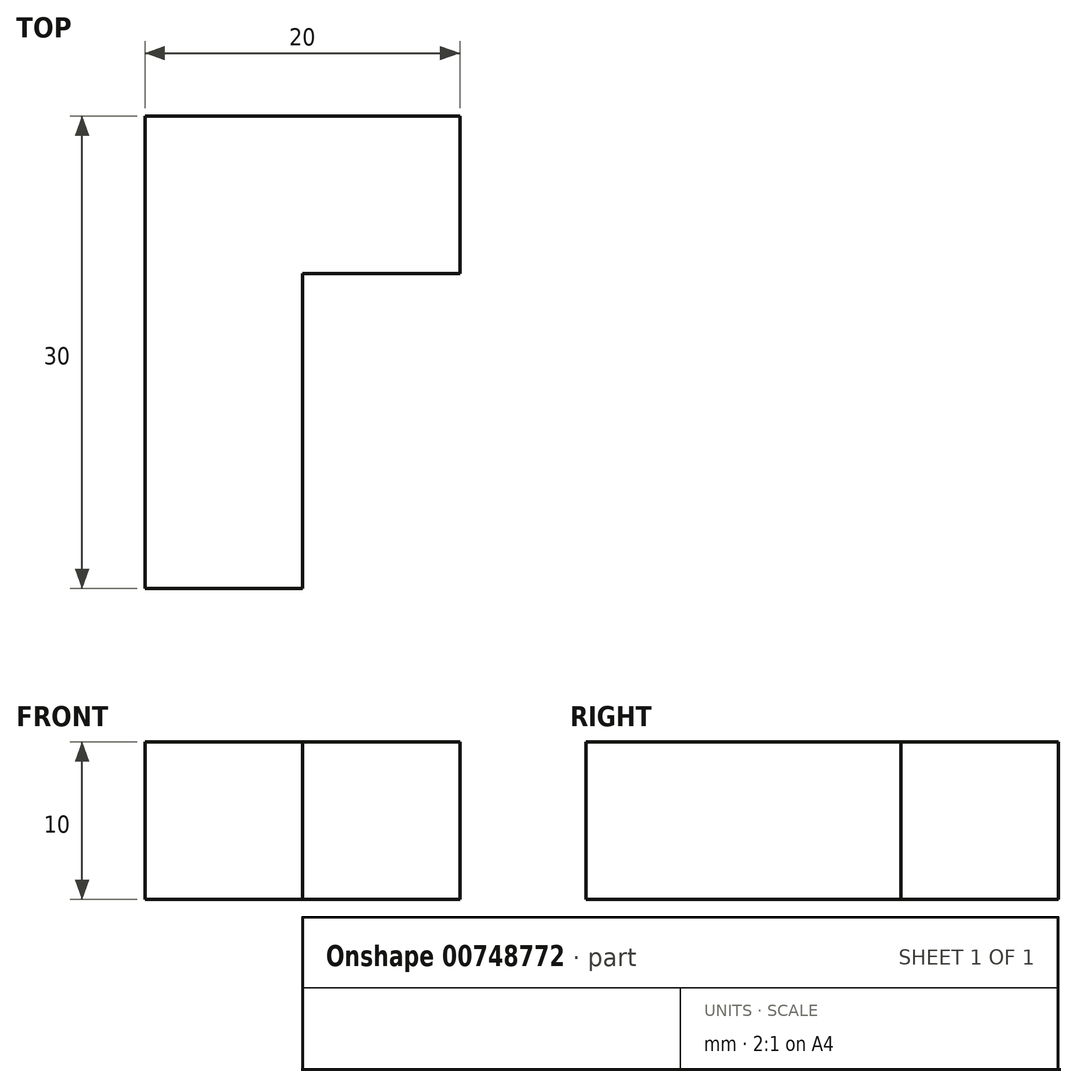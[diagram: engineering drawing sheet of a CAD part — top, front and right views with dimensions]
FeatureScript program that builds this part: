
annotation { "Feature Type Name" : "Feature", "Feature Type Description" : "" }
export const myFeature = defineFeature(function(context is Context, id is Id, definition is map)
    precondition{}
    {
        {
            var Q0;
            Q0=qCreatedBy(makeId("Top.planeOp"),FACE);
            var sketch = newSketch(context, id + "F0", { "sketchPlane" : qUnion([Q0])});
            skLineSegment(sketch, "E0.bottom", {"start": v(-49.52, 42.56) * mm, "end": v(-39.52, 42.56) * mm});
            skLineSegment(sketch, "E0.top", {"start": v(-49.52, 32.56) * mm, "end": v(-39.52, 32.56) * mm});
            skLineSegment(sketch, "E0.left", {"start": v(-49.52, 42.56) * mm, "end": v(-49.52, 32.56) * mm});
            skLineSegment(sketch, "E0.right", {"start": v(-39.52, 42.56) * mm, "end": v(-39.52, 32.56) * mm});
            skLineSegment(sketch, "E1.bottom", {"start": v(-39.52, 42.56) * mm, "end": v(-29.52, 42.56) * mm});
            skLineSegment(sketch, "E1.top", {"start": v(-39.52, 32.56) * mm, "end": v(-29.52, 32.56) * mm});
            skLineSegment(sketch, "E1.right", {"start": v(-29.52, 42.56) * mm, "end": v(-29.52, 32.56) * mm});
            skLineSegment(sketch, "E2.top", {"start": v(-49.52, 22.56) * mm, "end": v(-39.52, 22.56) * mm});
            skLineSegment(sketch, "E2.left", {"start": v(-49.52, 32.56) * mm, "end": v(-49.52, 22.56) * mm});
            skLineSegment(sketch, "E2.right", {"start": v(-39.52, 32.56) * mm, "end": v(-39.52, 22.56) * mm});
            skLineSegment(sketch, "E3.top", {"start": v(-49.52, 12.56) * mm, "end": v(-39.52, 12.56) * mm});
            skLineSegment(sketch, "E3.left", {"start": v(-49.52, 22.56) * mm, "end": v(-49.52, 12.56) * mm});
            skLineSegment(sketch, "E3.right", {"start": v(-39.52, 22.56) * mm, "end": v(-39.52, 12.56) * mm});
            skSolve(sketch);
        }
        {
            var Q0;
            Q0 = qSketchRegion(id + "F0", true);
            extrude(context, id + "F1", {"entities" : qUnion([Q0]), "depth" : 10 * mm, "offsetDistance" : 25 * mm});
        }
    });
